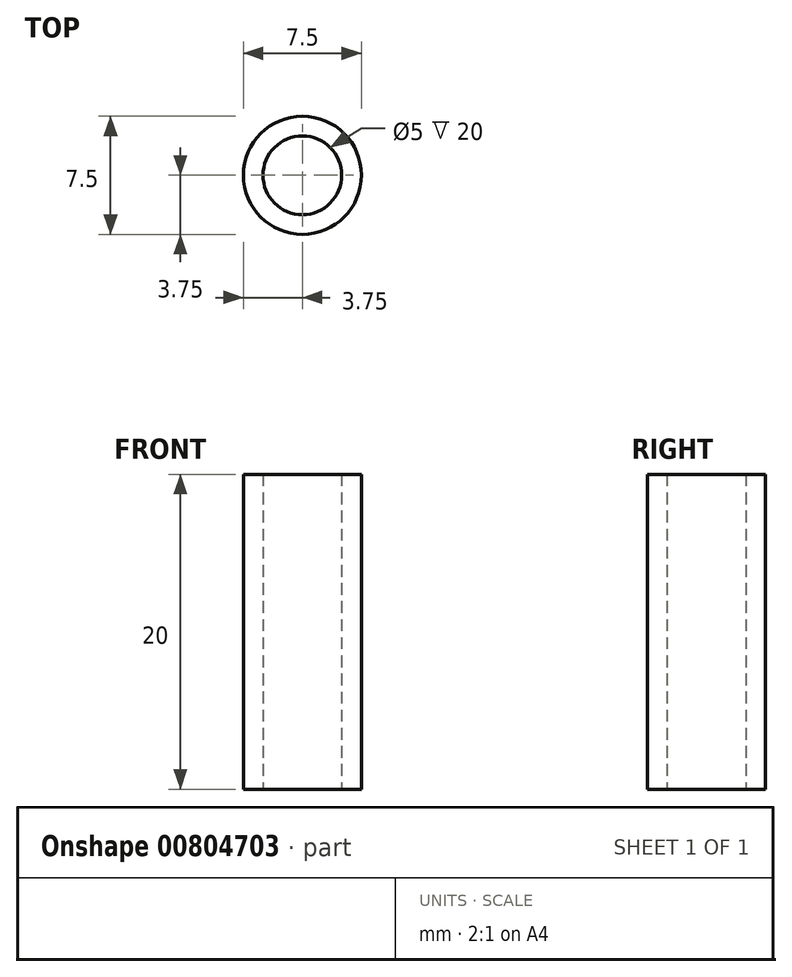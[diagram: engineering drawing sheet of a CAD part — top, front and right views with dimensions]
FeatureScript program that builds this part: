
annotation { "Feature Type Name" : "Feature", "Feature Type Description" : "" }
export const myFeature = defineFeature(function(context is Context, id is Id, definition is map)
    precondition{}
    {
        {
            var Q0;
            Q0=qCreatedBy(makeId("Top.planeOp"),FACE);
            var sketch = newSketch(context, id + "F0", { "sketchPlane" : qUnion([Q0])});
            skCircle(sketch, "E0", {"center": v(0, 0) * mm, "radius": 3.75 * mm});
            skCircle(sketch, "E1", {"center": v(0, 0) * mm, "radius": 2.5 * mm});
            skSolve(sketch);
        }
        {
            var Q0;
            Q0=qSketchRegion(id+"F0",true);
            extrude(context, id + "F1", {"entities" : qUnion([Q0]), "depth" : 20 * mm, "offsetDistance" : 25 * mm});
        }
    });
